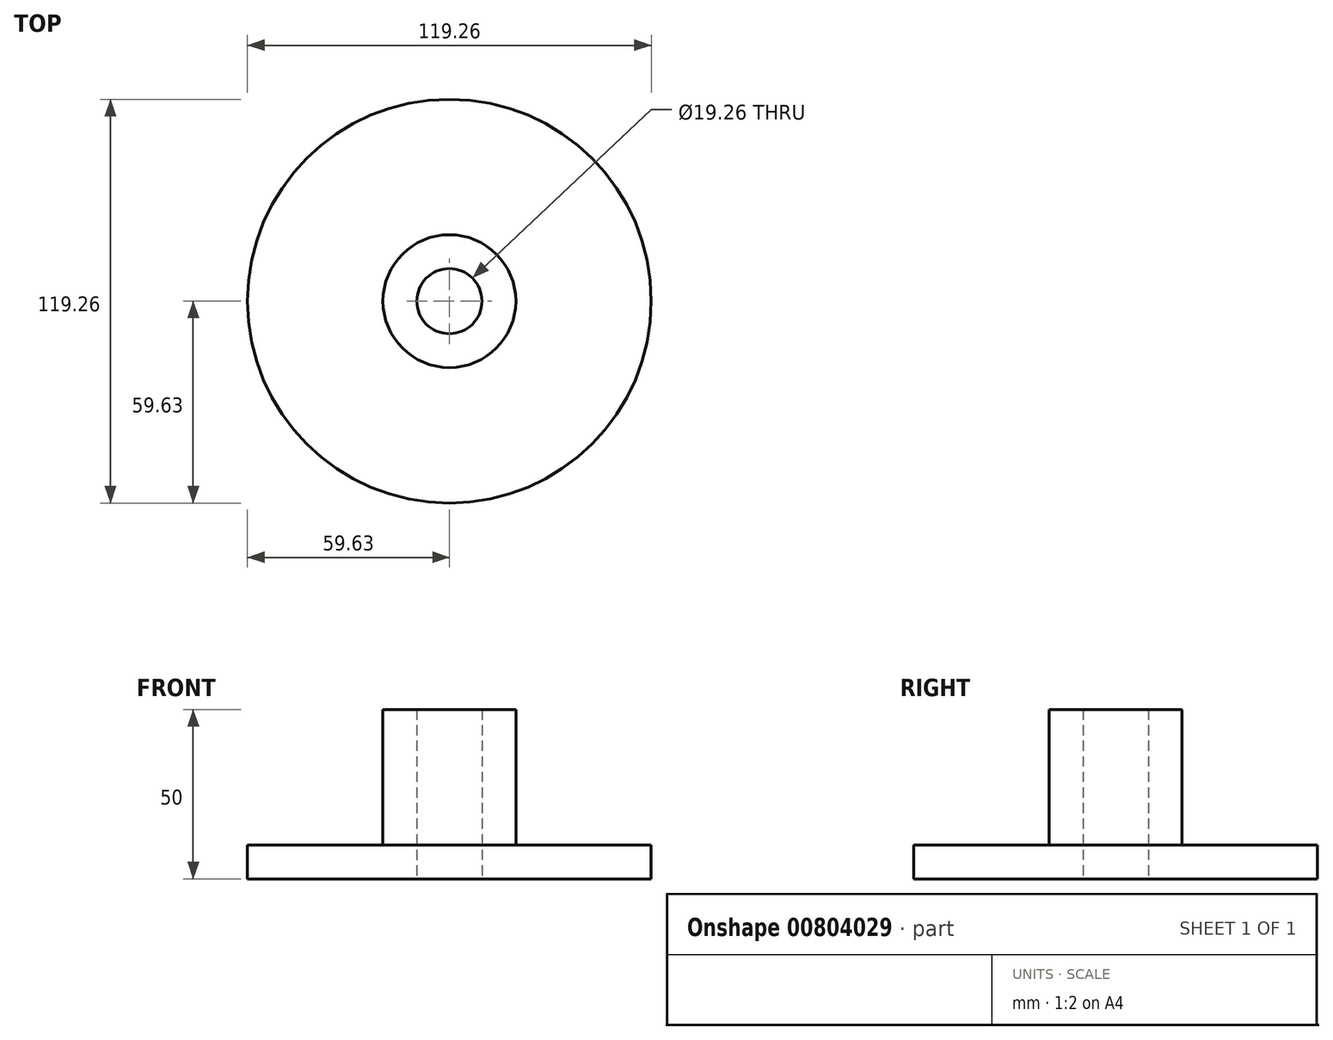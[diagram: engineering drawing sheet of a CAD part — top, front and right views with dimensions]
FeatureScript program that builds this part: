
annotation { "Feature Type Name" : "Feature", "Feature Type Description" : "" }
export const myFeature = defineFeature(function(context is Context, id is Id, definition is map)
    precondition{}
    {
        {
            var Q0;
            Q0=qCreatedBy(makeId("Front.planeOp"),FACE);
            var sketch = newSketch(context, id + "F0", { "sketchPlane" : qUnion([Q0])});
            skLineSegment(sketch, "E0", {"start": v(9.63, 0.3) * mm, "end": v(9.63, 50.3) * mm});
            skLineSegment(sketch, "E1", {"start": v(9.63, 50.3) * mm, "end": v(19.63, 50.3) * mm});
            skLineSegment(sketch, "E2", {"start": v(19.63, 50.3) * mm, "end": v(19.63, 10.3) * mm});
            skLineSegment(sketch, "E3", {"start": v(19.63, 10.3) * mm, "end": v(59.63, 10.3) * mm});
            skLineSegment(sketch, "E4", {"start": v(59.63, 0.31) * mm, "end": v(9.63, 0.3) * mm});
            skLineSegment(sketch, "E5", {"start": v(59.63, 0.31) * mm, "end": v(59.63, 10.31) * mm});
            skLineSegment(sketch, "E6", {"start": v(0, 0) * mm, "end": v(0, 62.09) * mm, "construction": true});
            skSolve(sketch);
        }
        {
            var Q0;
            Q0 = qSketchRegion(id + "F0", true);
            var Q1;
            Q1=sQuery(id+"F0.wireOp",EDGE,"E6");
            revolve(context, id + "F1", {"surfaceOperationType" : NewSurfaceOperationType.NEW, "entities" : qUnion([Q0]), "axis" : qUnion([Q1]), "revolveType" : RevolveType.FULL});
        }
    });
